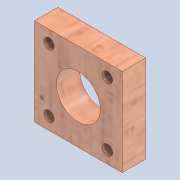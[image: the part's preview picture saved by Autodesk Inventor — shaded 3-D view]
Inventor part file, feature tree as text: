
AUTODESK INVENTOR PART (.ipt)
format: ipt  version: 2020 (Build 240168000, 168)  size: 197,120 bytes
history: native  units: mm
features: extrude x3, sketch x3
ambient origin geometry x8: Origin, YZ Plane, XZ Plane, XY Plane, X Axis, Y Axis, Z Axis, Center Point
bodies: Solid1 (feature_tree)
feature tree (6):
  extrude  "Extrusion1"  Depth=30.0mm
  extrude  "Extrusion2"  TaperAngle=0.0deg  [1 undecoded]
  extrude  "Extrusion3"  TaperAngle=0.0deg  [1 undecoded]
  sketch  "Sketch1"  dims[d0=30.0mm d1=30.0mm]
  sketch  "Sketch2"  dims[d2=8.0mm d3=0.0mm d6=0.0mm d7=0.0mm]
  sketch  "Sketch3"  dims[d9=3.5mm d15=0.0mm d16=0.0mm d17=15.0mm d19=10.75mm d20=10.75mm d21=20.0mm d22=21.5mm]
note: 2 required parameter values undecoded (feature->parameter linkage not recoverable at this tier; creation-order binding heuristic only, values carry confidence <= 0.55)
